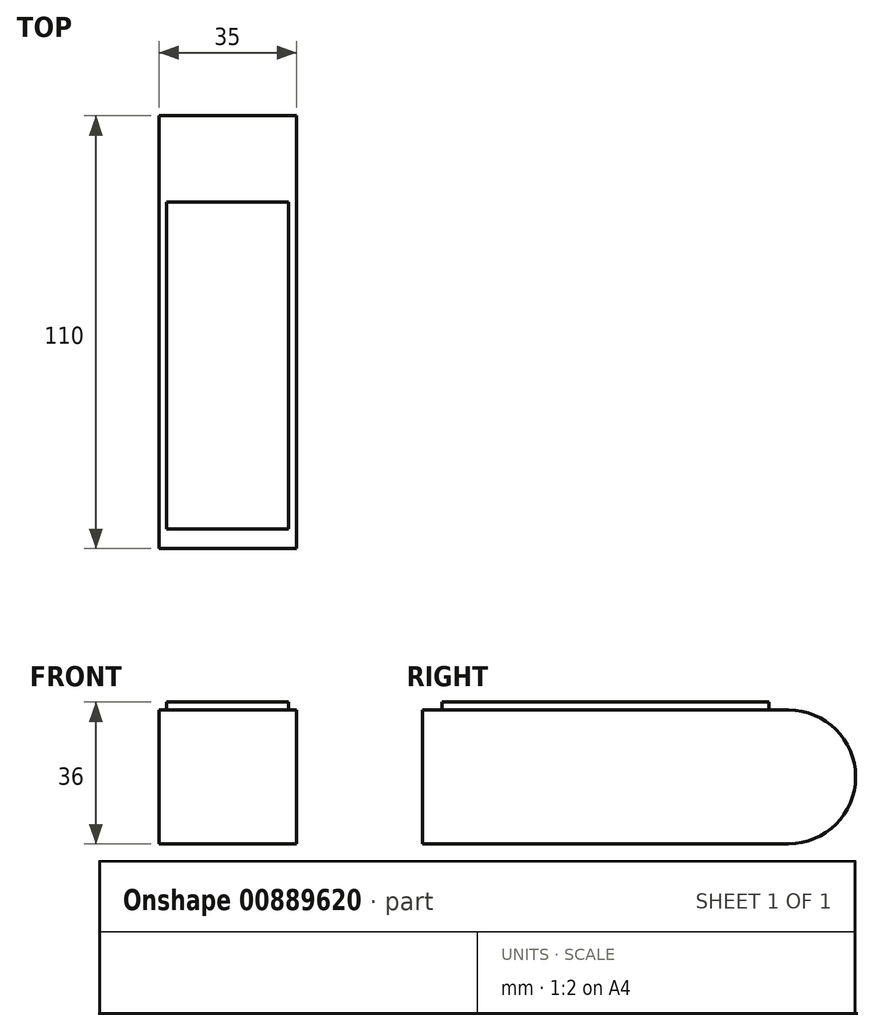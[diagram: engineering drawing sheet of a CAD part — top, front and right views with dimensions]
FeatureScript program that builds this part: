
annotation { "Feature Type Name" : "Feature", "Feature Type Description" : "" }
export const myFeature = defineFeature(function(context is Context, id is Id, definition is map)
    precondition{}
    {
        {
            assignVariable(context, id + "F0", {"name" : "body_w", "anyValue" : 35});
        }
        {
            var Q0;
            Q0=qCreatedBy(makeId("Right.planeOp"),FACE);
            var sketch = newSketch(context, id + "F1", { "sketchPlane" : qUnion([Q0])});
            skLineSegment(sketch, "E0.bottom", {"start": v(0, 17) * mm, "end": v(110, 17) * mm});
            skLineSegment(sketch, "E0.top", {"start": v(0, -17) * mm, "end": v(110, -17) * mm});
            skLineSegment(sketch, "E0.left", {"start": v(0, 17) * mm, "end": v(0, -17) * mm});
            skLineSegment(sketch, "E0.right", {"start": v(110, 17) * mm, "end": v(110, -17) * mm, "construction": true});
            skPoint(sketch, "E1", {"position": v(55, 17) * mm});
            skArc(sketch, "E2", {"start": v(93, -17) * mm, "mid": v(110, 0) * mm, "end": v(93, 17) * mm});
            skSolve(sketch);
        }
        {
            var Q0;
            Q0=qCreatedBy(makeId("Right.planeOp"),FACE);
            var sketch = newSketch(context, id + "F2", { "sketchPlane" : qUnion([Q0])});
            skLineSegment(sketch, "E3.bottom", {"start": v(5, 19) * mm, "end": v(88, 19) * mm});
            skLineSegment(sketch, "E3.top", {"start": v(5, 17) * mm, "end": v(88, 17) * mm});
            skLineSegment(sketch, "E3.left", {"start": v(5, 19) * mm, "end": v(5, 17) * mm});
            skLineSegment(sketch, "E3.right", {"start": v(88, 19) * mm, "end": v(88, 17) * mm});
            skPoint(sketch, "E4", {"position": v(55, 19) * mm});
            skPoint(sketch, "E5", {"position": v(0, 19) * mm});
            skLineSegment(sketch, "E6", {"start": v(55, 19) * mm, "end": v(55, 17) * mm, "construction": true});
            skSolve(sketch);
        }
        {
            var Q0;
            Q0=makeQuery(id+"F1.imprint","IMPRINT",FACE,{"disambiguationData":[TD([[makeQuery(id+"F1.imprint","IMPRINT",EDGE,{"derivedFrom":sQuery(id+"F1.wireOp",EDGE,"E0.bottom")}),-1.0]])]});
            extrude(context, id + "F3", {"entities" : qUnion([Q0]), "endBound" : BoundingType.SYMMETRIC, "depth" : (getVariable(context, 'body_w')) * mm, "offsetDistance" : 25 * mm});
        }
        {
            var Q0;
            Q0=makeQuery(id+"F2.imprint","IMPRINT",FACE,{"disambiguationData":[TD([[makeQuery(id+"F2.imprint","IMPRINT",EDGE,{"derivedFrom":sQuery(id+"F2.wireOp",EDGE,"E3.bottom")}),-1.0]])]});
            extrude(context, id + "F4", {"entities" : qUnion([Q0]), "endBound" : BoundingType.SYMMETRIC, "depth" : (getVariable(context, 'body_w') - 4) * mm, "offsetDistance" : 25 * mm});
        }
    });
